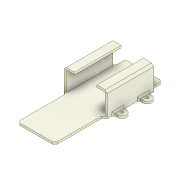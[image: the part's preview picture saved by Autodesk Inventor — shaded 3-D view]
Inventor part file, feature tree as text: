
AUTODESK INVENTOR PART (.ipt)
format: ipt  version: 2022 (Build 260153000, 153)  size: 233,984 bytes
history: native  units: mm
features: chamfer x4, sketch x3, extrude x2, thicken_offset x2, hole x1, projected_geometry x1
ambient origin geometry x8: Origin, YZ Plane, XZ Plane, XY Plane, X Axis, Y Axis, Z Axis, Center Point
bodies: Solid1 (feature_tree)
feature tree (13):
  extrude  "Extrusion1"  Depth=34.0mm
  hole  "Hole1"  [1 undecoded]
  extrude  "Extrusion2"  Depth=3.0mm TaperAngle=0.0deg
  chamfer  "Chamfer2"  Distance=4.0mm
  chamfer  "Chamfer3"  Distance=4.0mm
  chamfer  "Chamfer4"  Distance=4.0mm
  chamfer  "Chamfer5"  Distance=25.5mm
  thicken_offset  "Thicken3"
  thicken_offset  "Thicken4"
  sketch  "Sketch1"  dims[d0=34.0mm d1=69.0mm]
  sketch  "Sketch2"  dims[d2=50.0mm d3=10.0mm]
  sketch  "Sketch5"  dims[d4=6.0mm d5=3.0mm d6=0.0mm d7=3.4mm d8=6.0mm d9=4.0mm d10=2.0mm d11=90.0deg d12=6.0mm d13=0.0mm d14=4.0mm d20=4.0mm d21=4.0mm d22=25.5mm d23=10.0mm d24=3.0mm d25=0.0mm d29=2.0mm d30=2.0mm d31=45.0deg d32=3.0mm d33=2.0mm d34=45.0deg d35=3.7037mm d36=2.0mm d37=45.0deg d38=3.0mm d39=2.0mm d40=45.0deg d41=145.0mm d42=15.5mm d43=4.0mm d48=1.0mm d49=1.0mm d50=1.0mm d51=1.0mm]
  projected_geometry  "Project Cut Edges2"
note: 1 required parameter value undecoded (feature->parameter linkage not recoverable at this tier; creation-order binding heuristic only, values carry confidence <= 0.55)
